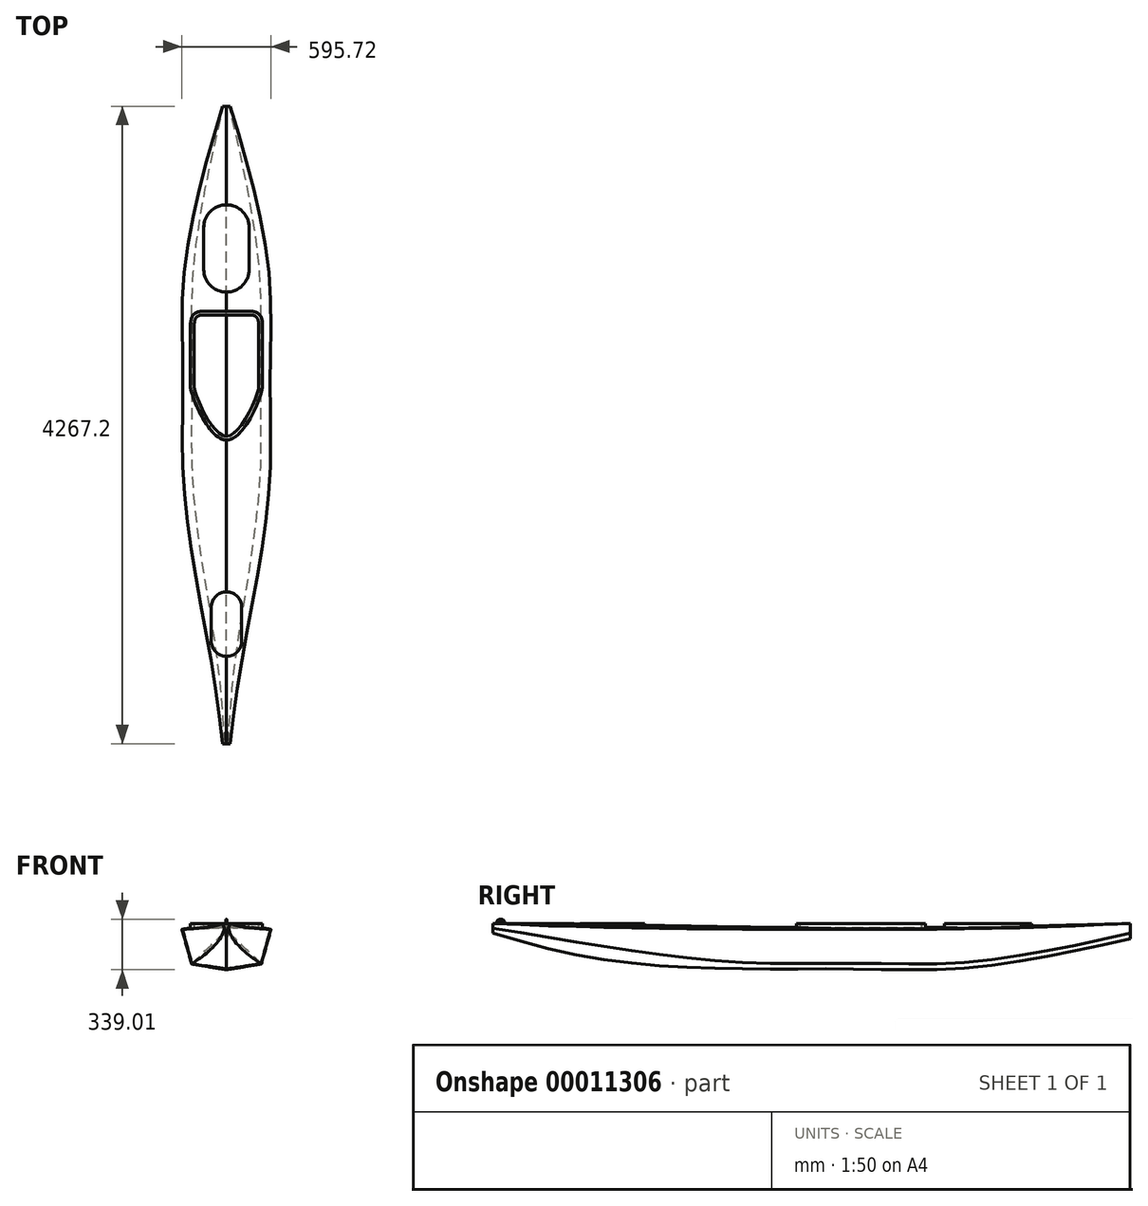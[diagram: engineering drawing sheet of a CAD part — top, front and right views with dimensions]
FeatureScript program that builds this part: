
annotation { "Feature Type Name" : "Feature", "Feature Type Description" : "" }
export const myFeature = defineFeature(function(context is Context, id is Id, definition is map)
    precondition{}
    {
        {
            var Q0;
            Q0=qCreatedBy(makeId("Front.planeOp"),FACE);
            var sketch = newSketch(context, id + "F0", { "sketchPlane" : qUnion([Q0])});
            skLineSegment(sketch, "E0", {"start": v(0, 0) * mm, "end": v(25.4, 0) * mm});
            skLineSegment(sketch, "E1", {"start": v(25.4, 0) * mm, "end": v(12.7, -31.75) * mm});
            skLineSegment(sketch, "E2.0.MirrorCS", {"start": v(0, 0) * mm, "end": v(-25.4, 0) * mm});
            skLineSegment(sketch, "E3.0.MirrorCS", {"start": v(-25.4, 0) * mm, "end": v(-12.7, -31.75) * mm});
            skPoint(sketch, "E4", {"position": v(12.7, -31.75) * mm});
            skPoint(sketch, "E5.0.MirrorP", {"position": v(-12.7, -31.75) * mm});
            skLineSegment(sketch, "E6", {"start": v(12.7, -31.75) * mm, "end": v(0, -63.5) * mm});
            skLineSegment(sketch, "E7", {"start": v(-12.7, -31.75) * mm, "end": v(0, -63.5) * mm});
            skSolve(sketch);
        }
        {
            var Q0;
            Q0=qCreatedBy(makeId("Front.planeOp"),FACE);
            cPlane(context, id + "F1", {"entities" : qUnion([Q0]), "cplaneType" : CPlaneType.OFFSET, "offset" : 304.8 * mm, "oppositeDirection" : true, "width" : 152.4 * mm, "height" : 152.4 * mm});
        }
        {
            var Q0;
            Q0=qCreatedBy(id+"F1.planeOp",FACE);
            var sketch = newSketch(context, id + "F2", { "sketchPlane" : qUnion([Q0])});
            skLineSegment(sketch, "E8", {"start": v(0, 0) * mm, "end": v(63.5, -12.7) * mm});
            skLineSegment(sketch, "E9", {"start": v(63.5, -12.7) * mm, "end": v(31.75, -82.55) * mm});
            skLineSegment(sketch, "E10.0.MirrorCS", {"start": v(0, 0) * mm, "end": v(-63.5, -12.7) * mm});
            skLineSegment(sketch, "E11.0.MirrorCS", {"start": v(-63.5, -12.7) * mm, "end": v(-31.75, -82.55) * mm});
            skPoint(sketch, "E12", {"position": v(31.75, -82.55) * mm});
            skPoint(sketch, "E13.0.MirrorP", {"position": v(-31.75, -82.55) * mm});
            skLineSegment(sketch, "E14", {"start": v(31.75, -82.55) * mm, "end": v(0, -152.4) * mm});
            skLineSegment(sketch, "E15", {"start": v(-31.75, -82.55) * mm, "end": v(0, -152.4) * mm});
            skSolve(sketch);
        }
        {
            var Q0;
            Q0=qCreatedBy(id+"F1.planeOp",FACE);
            cPlane(context, id + "F3", {"entities" : qUnion([Q0]), "cplaneType" : CPlaneType.OFFSET, "offset" : 304.8 * mm, "oppositeDirection" : true, "width" : 152.4 * mm, "height" : 152.4 * mm});
        }
        {
            var Q0;
            Q0=qCreatedBy(id+"F3.planeOp",FACE);
            var sketch = newSketch(context, id + "F4", { "sketchPlane" : qUnion([Q0])});
            skLineSegment(sketch, "E16", {"start": v(0, 0) * mm, "end": v(228.6, -25.4) * mm});
            skLineSegment(sketch, "E17", {"start": v(228.6, -25.4) * mm, "end": v(152.4, -152.4) * mm});
            skLineSegment(sketch, "E18", {"start": v(152.4, -152.4) * mm, "end": v(0, -203.2) * mm});
            skLineSegment(sketch, "E19.0.MirrorCS", {"start": v(0, 0) * mm, "end": v(-228.6, -25.4) * mm});
            skLineSegment(sketch, "E20.0.MirrorCS", {"start": v(-228.6, -25.4) * mm, "end": v(-152.4, -152.4) * mm});
            skLineSegment(sketch, "E21.0.MirrorCS", {"start": v(-152.4, -152.4) * mm, "end": v(0, -203.2) * mm});
            skSolve(sketch);
        }
        {
            var Q0;
            Q0=qCreatedBy(id+"F3.planeOp",FACE);
            cPlane(context, id + "F5", {"entities" : qUnion([Q0]), "cplaneType" : CPlaneType.OFFSET, "offset" : 304.8 * mm, "oppositeDirection" : true, "width" : 152.4 * mm, "height" : 152.4 * mm});
        }
        {
            var Q0;
            Q0=qCreatedBy(id+"F5.planeOp",FACE);
            var sketch = newSketch(context, id + "F6", { "sketchPlane" : qUnion([Q0])});
            skLineSegment(sketch, "E22", {"start": v(0, 0) * mm, "end": v(254, -31.75) * mm});
            skLineSegment(sketch, "E23", {"start": v(254, -31.75) * mm, "end": v(190.5, -190.5) * mm});
            skLineSegment(sketch, "E24", {"start": v(190.5, -190.5) * mm, "end": v(0, -241.3) * mm});
            skLineSegment(sketch, "E25.0.MirrorCS", {"start": v(0, 0) * mm, "end": v(-254, -31.75) * mm});
            skLineSegment(sketch, "E26.0.MirrorCS", {"start": v(-254, -31.75) * mm, "end": v(-190.5, -190.5) * mm});
            skLineSegment(sketch, "E27.0.MirrorCS", {"start": v(-190.5, -190.5) * mm, "end": v(0, -241.3) * mm});
            skSolve(sketch);
        }
        {
            var Q0;
            Q0=qCreatedBy(id+"F5.planeOp",FACE);
            cPlane(context, id + "F7", {"entities" : qUnion([Q0]), "cplaneType" : CPlaneType.OFFSET, "offset" : 304.8 * mm, "oppositeDirection" : true, "width" : 152.4 * mm, "height" : 152.4 * mm});
        }
        {
            var Q0;
            Q0=qCreatedBy(id+"F7.planeOp",FACE);
            var sketch = newSketch(context, id + "F8", { "sketchPlane" : qUnion([Q0])});
            skLineSegment(sketch, "E28", {"start": v(0, -12.7) * mm, "end": v(279.4, -38.1) * mm});
            skLineSegment(sketch, "E29", {"start": v(279.4, -38.1) * mm, "end": v(228.6, -203.2) * mm});
            skLineSegment(sketch, "E30", {"start": v(228.6, -203.2) * mm, "end": v(0, -266.7) * mm});
            skLineSegment(sketch, "E31.0.MirrorCS", {"start": v(0, -12.7) * mm, "end": v(-279.4, -38.1) * mm});
            skLineSegment(sketch, "E32.0.MirrorCS", {"start": v(-279.4, -38.1) * mm, "end": v(-228.6, -203.2) * mm});
            skLineSegment(sketch, "E33.0.MirrorCS", {"start": v(-228.6, -203.2) * mm, "end": v(0, -266.7) * mm});
            skSolve(sketch);
        }
        {
            var Q0;
            Q0=qCreatedBy(id+"F7.planeOp",FACE);
            cPlane(context, id + "F9", {"entities" : qUnion([Q0]), "cplaneType" : CPlaneType.OFFSET, "offset" : 304.8 * mm, "oppositeDirection" : true, "width" : 152.4 * mm, "height" : 152.4 * mm});
        }
        {
            var Q0;
            Q0=qCreatedBy(id+"F9.planeOp",FACE);
            var sketch = newSketch(context, id + "F10", { "sketchPlane" : qUnion([Q0])});
            skLineSegment(sketch, "E34", {"start": v(0, -25.4) * mm, "end": v(292.1, -38.1) * mm});
            skLineSegment(sketch, "E35", {"start": v(292.1, -38.1) * mm, "end": v(228.6, -228.6) * mm});
            skLineSegment(sketch, "E36", {"start": v(228.6, -228.6) * mm, "end": v(0, -292.1) * mm});
            skLineSegment(sketch, "E37.0.MirrorCS", {"start": v(0, -25.4) * mm, "end": v(-292.1, -38.1) * mm});
            skLineSegment(sketch, "E38.0.MirrorCS", {"start": v(-292.1, -38.1) * mm, "end": v(-228.6, -228.6) * mm});
            skLineSegment(sketch, "E39.0.MirrorCS", {"start": v(-228.6, -228.6) * mm, "end": v(0, -292.1) * mm});
            skSolve(sketch);
        }
        {
            var Q0;
            Q0=qCreatedBy(id+"F9.planeOp",FACE);
            cPlane(context, id + "F11", {"entities" : qUnion([Q0]), "cplaneType" : CPlaneType.OFFSET, "offset" : 304.8 * mm, "oppositeDirection" : true, "width" : 152.4 * mm, "height" : 152.4 * mm});
        }
        {
            var Q0;
            Q0=qCreatedBy(id+"F11.planeOp",FACE);
            var sketch = newSketch(context, id + "F12", { "sketchPlane" : qUnion([Q0])});
            skLineSegment(sketch, "E40", {"start": v(0, -25.4) * mm, "end": v(292.1, -38.1) * mm});
            skLineSegment(sketch, "E41", {"start": v(292.1, -38.1) * mm, "end": v(228.6, -266.7) * mm});
            skLineSegment(sketch, "E42", {"start": v(228.6, -266.7) * mm, "end": v(0, -304.8) * mm});
            skLineSegment(sketch, "E43.0.MirrorCS", {"start": v(0, -25.4) * mm, "end": v(-292.1, -38.1) * mm});
            skLineSegment(sketch, "E44.0.MirrorCS", {"start": v(-292.1, -38.1) * mm, "end": v(-228.6, -266.7) * mm});
            skLineSegment(sketch, "E45.0.MirrorCS", {"start": v(-228.6, -266.7) * mm, "end": v(0, -304.8) * mm});
            skSolve(sketch);
        }
        {
            var Q0;
            Q0=qCreatedBy(id+"F11.planeOp",FACE);
            cPlane(context, id + "F13", {"entities" : qUnion([Q0]), "cplaneType" : CPlaneType.OFFSET, "offset" : 304.8 * mm, "oppositeDirection" : true, "width" : 152.4 * mm, "height" : 152.4 * mm});
        }
        {
            var Q0;
            Q0=qCreatedBy(id+"F13.planeOp",FACE);
            var sketch = newSketch(context, id + "F14", { "sketchPlane" : qUnion([Q0])});
            skLineSegment(sketch, "E46.0.0", {"start": v(292.1, -38.1) * mm, "end": v(0, -25.4) * mm});
            skLineSegment(sketch, "E46.0.1", {"start": v(0, -25.4) * mm, "end": v(-292.1, -38.1) * mm});
            skLineSegment(sketch, "E46.0.2", {"start": v(-292.1, -38.1) * mm, "end": v(-228.6, -266.7) * mm});
            skLineSegment(sketch, "E46.0.3", {"start": v(-228.6, -266.7) * mm, "end": v(0, -304.8) * mm});
            skLineSegment(sketch, "E46.0.4", {"start": v(0, -304.8) * mm, "end": v(228.6, -266.7) * mm});
            skLineSegment(sketch, "E46.0.5", {"start": v(228.6, -266.7) * mm, "end": v(292.1, -38.1) * mm});
            skSolve(sketch);
        }
        {
            var Q0;
            Q0=qCreatedBy(id+"F13.planeOp",FACE);
            cPlane(context, id + "F15", {"entities" : qUnion([Q0]), "cplaneType" : CPlaneType.OFFSET, "offset" : 304.8 * mm, "oppositeDirection" : true, "width" : 152.4 * mm, "height" : 152.4 * mm});
        }
        {
            var Q0;
            Q0=qCreatedBy(id+"F15.planeOp",FACE);
            var sketch = newSketch(context, id + "F16", { "sketchPlane" : qUnion([Q0])});
            skLineSegment(sketch, "E47.0.0", {"start": v(228.6, -266.7) * mm, "end": v(292.1, -38.1) * mm});
            skLineSegment(sketch, "E47.0.1", {"start": v(292.1, -38.1) * mm, "end": v(0, -25.4) * mm});
            skLineSegment(sketch, "E47.0.2", {"start": v(0, -25.4) * mm, "end": v(-292.1, -38.1) * mm});
            skLineSegment(sketch, "E47.0.3", {"start": v(-292.1, -38.1) * mm, "end": v(-228.6, -266.7) * mm});
            skLineSegment(sketch, "E47.0.4", {"start": v(-228.6, -266.7) * mm, "end": v(0, -304.8) * mm});
            skLineSegment(sketch, "E47.0.5", {"start": v(0, -304.8) * mm, "end": v(228.6, -266.7) * mm});
            skSolve(sketch);
        }
        {
            var Q0;
            Q0=qCreatedBy(id+"F15.planeOp",FACE);
            cPlane(context, id + "F17", {"entities" : qUnion([Q0]), "cplaneType" : CPlaneType.OFFSET, "offset" : 304.8 * mm, "oppositeDirection" : true, "width" : 152.4 * mm, "height" : 152.4 * mm});
        }
        {
            var Q0;
            Q0=qCreatedBy(id+"F17.planeOp",FACE);
            var sketch = newSketch(context, id + "F18", { "sketchPlane" : qUnion([Q0])});
            skLineSegment(sketch, "E48.0.0", {"start": v(0, -304.8) * mm, "end": v(228.6, -266.7) * mm});
            skLineSegment(sketch, "E48.0.1", {"start": v(228.6, -266.7) * mm, "end": v(292.1, -38.1) * mm});
            skLineSegment(sketch, "E48.0.2", {"start": v(292.1, -38.1) * mm, "end": v(0, -25.4) * mm});
            skLineSegment(sketch, "E48.0.3", {"start": v(0, -25.4) * mm, "end": v(-292.1, -38.1) * mm});
            skLineSegment(sketch, "E48.0.4", {"start": v(-292.1, -38.1) * mm, "end": v(-228.6, -266.7) * mm});
            skLineSegment(sketch, "E48.0.5", {"start": v(-228.6, -266.7) * mm, "end": v(0, -304.8) * mm});
            skSolve(sketch);
        }
        {
            var Q0;
            Q0=qCreatedBy(id+"F17.planeOp",FACE);
            cPlane(context, id + "F19", {"entities" : qUnion([Q0]), "cplaneType" : CPlaneType.OFFSET, "offset" : 304.8 * mm, "oppositeDirection" : true, "width" : 152.4 * mm, "height" : 152.4 * mm});
        }
        {
            var Q0;
            Q0=qCreatedBy(id+"F19.planeOp",FACE);
            var sketch = newSketch(context, id + "F20", { "sketchPlane" : qUnion([Q0])});
            skLineSegment(sketch, "E49.0.0", {"start": v(-228.6, -266.7) * mm, "end": v(0, -304.8) * mm});
            skLineSegment(sketch, "E49.0.1", {"start": v(0, -304.8) * mm, "end": v(228.6, -266.7) * mm});
            skLineSegment(sketch, "E49.0.2", {"start": v(228.6, -266.7) * mm, "end": v(292.1, -38.1) * mm});
            skLineSegment(sketch, "E49.0.3", {"start": v(292.1, -38.1) * mm, "end": v(0, -25.4) * mm});
            skLineSegment(sketch, "E49.0.4", {"start": v(0, -25.4) * mm, "end": v(-292.1, -38.1) * mm});
            skLineSegment(sketch, "E49.0.5", {"start": v(-292.1, -38.1) * mm, "end": v(-228.6, -266.7) * mm});
            skSolve(sketch);
        }
        {
            var Q0;
            Q0=qCreatedBy(id+"F19.planeOp",FACE);
            cPlane(context, id + "F21", {"entities" : qUnion([Q0]), "cplaneType" : CPlaneType.OFFSET, "offset" : 1219.2 * mm, "oppositeDirection" : true, "width" : 152.4 * mm, "height" : 152.4 * mm});
        }
        {
            var Q0;
            Q0=qCreatedBy(id+"F21.planeOp",FACE);
            var sketch = newSketch(context, id + "F22", { "sketchPlane" : qUnion([Q0])});
            skLineSegment(sketch, "E50", {"start": v(0, 0) * mm, "end": v(25.4, 0) * mm});
            skLineSegment(sketch, "E51", {"start": v(25.4, 0) * mm, "end": v(19.05, -63.5) * mm});
            skLineSegment(sketch, "E52", {"start": v(19.05, -63.5) * mm, "end": v(0, -101.6) * mm});
            skLineSegment(sketch, "E53.0.MirrorCS", {"start": v(0, 0) * mm, "end": v(-25.4, 0) * mm});
            skLineSegment(sketch, "E54.0.MirrorCS", {"start": v(-25.4, 0) * mm, "end": v(-19.05, -63.5) * mm});
            skLineSegment(sketch, "E55.0.MirrorCS", {"start": v(-19.05, -63.5) * mm, "end": v(0, -101.6) * mm});
            skSolve(sketch);
        }
        {
            var Q0;
            Q0=makeQuery(id+"F0.imprint","IMPRINT",FACE,{"disambiguationData":[TD([[makeQuery(id+"F0.imprint","IMPRINT",EDGE,{"derivedFrom":sQuery(id+"F0.wireOp",EDGE,"E0")}),-1.0]])]});
            var Q1;
            Q1=makeQuery(id+"F2.imprint","IMPRINT",FACE,{"disambiguationData":[TD([[makeQuery(id+"F2.imprint","IMPRINT",EDGE,{"derivedFrom":sQuery(id+"F2.wireOp",EDGE,"E8")}),-1.0]])]});
            var Q2;
            Q2=makeQuery(id+"F12.imprint","IMPRINT",FACE,{"disambiguationData":[TD([[makeQuery(id+"F12.imprint","IMPRINT",EDGE,{"derivedFrom":sQuery(id+"F12.wireOp",EDGE,"E40")}),-1.0]])]});
            var Q3;
            Q3=makeQuery(id+"F16.imprint","IMPRINT",FACE,{"disambiguationData":[TD([[makeQuery(id+"F16.imprint","IMPRINT",EDGE,{"derivedFrom":sQuery(id+"F16.wireOp",EDGE,"E47.0.0")}),1.0]])]});
            var Q4;
            Q4=makeQuery(id+"F20.imprint","IMPRINT",FACE,{"disambiguationData":[TD([[makeQuery(id+"F20.imprint","IMPRINT",EDGE,{"derivedFrom":sQuery(id+"F20.wireOp",EDGE,"E49.0.0")}),1.0]])]});
            var Q5;
            Q5=makeQuery(id+"F22.imprint","IMPRINT",FACE,{"disambiguationData":[TD([[makeQuery(id+"F22.imprint","IMPRINT",EDGE,{"derivedFrom":sQuery(id+"F22.wireOp",EDGE,"E50")}),-1.0]])]});
            loft(context, id + "F23", {"sheetProfilesArray" : [{ "sheetProfileEntities" : qUnion([Q0]) }, { "sheetProfileEntities" : qUnion([Q1]) }, { "sheetProfileEntities" : qUnion([Q2]) }, { "sheetProfileEntities" : qUnion([Q3]) }, { "sheetProfileEntities" : qUnion([Q4]) }, { "sheetProfileEntities" : qUnion([Q5]) }]});
        }
        {
            var Q0;
            Q0=qCreatedBy(makeId("Right.planeOp"),FACE);
            var sketch = newSketch(context, id + "F24", { "sketchPlane" : qUnion([Q0])});
            skArc(sketch, "E56", {"start": v(76.2, 0) * mm, "mid": v(50.8, 25.94) * mm, "end": v(25.4, 0) * mm});
            skSolve(sketch);
        }
        {
            var Q0;
            Q0=qCreatedBy(makeId("Top.planeOp"),FACE);
            var sketch = newSketch(context, id + "F25", { "sketchPlane" : qUnion([Q0])});
            skPoint(sketch, "E57.0", {"position": v(0, 25.4) * mm});
            skCircle(sketch, "E58", {"center": v(0, 25.4) * mm, "radius": 3.18 * mm});
            skSolve(sketch);
        }
        {
            var Q0;
            Q0=qSketchRegion(id+"F25",true);
            var Q1;
            Q1=sQuery(id+"F24.wireOp",EDGE,"E56");
            sweep(context, id + "F26", {"operationType" : NewBodyOperationType.ADD, "profiles" : qUnion([Q0]), "path" : qUnion([Q1])});
        }
        {
            var Q0;
            Q0=qCreatedBy(makeId("Top.planeOp"),FACE);
            var sketch = newSketch(context, id + "F27", { "sketchPlane" : qUnion([Q0])});
            skLineSegment(sketch, "E59", {"start": v(0, 2895.6) * mm, "end": v(139.7, 2895.6) * mm});
            skLineSegment(sketch, "E60", {"start": v(241.3, 2794) * mm, "end": v(241.3, 2387.6) * mm});
            skPoint(sketch, "E61", {"position": v(241.3, 2387.6) * mm});
            skFitSpline(sketch, "E62", {"points": [v(139.7, 2895.6) * mm, v(241.3, 2794) * mm], "startDerivative": vector(228.6, 0) * mm, "endDerivative": vector(0, -228.6) * mm});
            skFitSpline(sketch, "E63", {"points": [v(241.3, 2387.6) * mm, v(0, 2032) * mm, v(-241.3, 2387.6) * mm], "startDerivative": vector(0, -304.8) * mm, "endDerivative": vector(0, 304.8) * mm});
            skLineSegment(sketch, "E64.0.MirrorCS", {"start": v(0, 2895.6) * mm, "end": v(-139.7, 2895.6) * mm});
            skFitSpline(sketch, "E65.0.MirrorCS", {"points": [v(-139.7, 2895.6) * mm, v(-241.3, 2794) * mm], "startDerivative": vector(-228.6, 0) * mm, "endDerivative": vector(0, -228.6) * mm});
            skLineSegment(sketch, "E66.0.MirrorCS", {"start": v(-241.3, 2794) * mm, "end": v(-241.3, 2387.6) * mm});
            skLineSegment(sketch, "E67.0", {"start": v(0, 2870.2) * mm, "end": v(-139.7, 2870.2) * mm});
            skLineSegment(sketch, "E67.1", {"start": v(0, 2870.2) * mm, "end": v(139.7, 2870.2) * mm});
            skFitSpline(sketch, "E67.2", {"points": [v(139.7, 2870.2) * mm, v(144.1, 2870.2) * mm, v(152.45, 2870.02) * mm, v(163.52, 2869.19) * mm, v(173.13, 2867.83) * mm, v(181.28, 2866) * mm, v(188, 2863.78) * mm, v(193.4, 2861.26) * mm, v(197.7, 2858.51) * mm, v(201.2, 2855.5) * mm, v(204.21, 2852) * mm, v(206.96, 2847.7) * mm, v(209.48, 2842.3) * mm, v(211.7, 2835.58) * mm, v(213.53, 2827.43) * mm, v(214.89, 2817.82) * mm, v(215.72, 2806.75) * mm, v(215.9, 2798.4) * mm, v(215.9, 2794) * mm]});
            skLineSegment(sketch, "E67.3", {"start": v(215.9, 2794) * mm, "end": v(215.9, 2387.6) * mm});
            skFitSpline(sketch, "E67.4", {"points": [v(215.9, 2387.6) * mm, v(215.9, 2387.43) * mm, v(215.88, 2386.78) * mm, v(215.73, 2385.04) * mm, v(215.43, 2382.7) * mm, v(214.8, 2378.9) * mm, v(213.58, 2373.03) * mm, v(211.45, 2364.52) * mm, v(208.69, 2354.76) * mm, v(204.18, 2340.3) * mm, v(197.1, 2319.87) * mm, v(186.46, 2292.58) * mm, v(173.9, 2263.39) * mm, v(159.63, 2233.19) * mm, v(143.84, 2202.84) * mm, v(126.75, 2173.2) * mm, v(108.6, 2145.15) * mm, v(89.68, 2119.56) * mm, v(73.53, 2101.04) * mm, v(60.62, 2088.33) * mm, v(51.02, 2079.96) * mm, v(41.58, 2072.85) * mm, v(32.4, 2067.05) * mm, v(25.06, 2063.36) * mm, v(19.41, 2061.1) * mm, v(15.3, 2059.72) * mm, v(11.3, 2058.67) * mm, v(7.44, 2057.93) * mm, v(4.3, 2057.57) * mm, v(1.83, 2057.42) * mm, v(0, 2057.39) * mm, v(-1.83, 2057.42) * mm, v(-4.3, 2057.57) * mm, v(-7.44, 2057.93) * mm, v(-11.3, 2058.67) * mm, v(-15.3, 2059.72) * mm, v(-19.41, 2061.1) * mm, v(-25.06, 2063.36) * mm, v(-32.4, 2067.05) * mm, v(-41.58, 2072.85) * mm, v(-51.02, 2079.96) * mm, v(-60.62, 2088.33) * mm, v(-73.53, 2101.04) * mm, v(-89.68, 2119.56) * mm, v(-108.6, 2145.15) * mm, v(-126.75, 2173.2) * mm, v(-143.84, 2202.84) * mm, v(-159.63, 2233.19) * mm, v(-173.9, 2263.39) * mm, v(-186.46, 2292.58) * mm, v(-197.1, 2319.87) * mm, v(-204.18, 2340.3) * mm, v(-208.69, 2354.76) * mm, v(-211.45, 2364.52) * mm, v(-213.58, 2373.03) * mm, v(-214.8, 2378.9) * mm, v(-215.43, 2382.7) * mm, v(-215.73, 2385.04) * mm, v(-215.88, 2386.78) * mm, v(-215.9, 2387.43) * mm, v(-215.9, 2387.6) * mm]});
            skFitSpline(sketch, "E67.5", {"points": [v(-139.7, 2870.2) * mm, v(-144.1, 2870.2) * mm, v(-152.45, 2870.02) * mm, v(-163.52, 2869.19) * mm, v(-173.13, 2867.83) * mm, v(-181.28, 2866) * mm, v(-188, 2863.78) * mm, v(-193.4, 2861.26) * mm, v(-197.7, 2858.51) * mm, v(-201.2, 2855.5) * mm, v(-204.21, 2852) * mm, v(-206.96, 2847.7) * mm, v(-209.48, 2842.3) * mm, v(-211.7, 2835.58) * mm, v(-213.53, 2827.43) * mm, v(-214.89, 2817.82) * mm, v(-215.72, 2806.75) * mm, v(-215.9, 2798.4) * mm, v(-215.9, 2794) * mm]});
            skLineSegment(sketch, "E67.6", {"start": v(-215.9, 2794) * mm, "end": v(-215.9, 2387.6) * mm});
            skFitSpline(sketch, "E68.0", {"points": [v(0, 3048) * mm, v(0, 3454.4) * mm, v(0, 3860.8) * mm, v(0, 4267.2) * mm], "construction": true});
            skArc(sketch, "E69", {"start": v(-152.4, 3175) * mm, "mid": v(-107.76, 3067.24) * mm, "end": v(0, 3022.6) * mm});
            skArc(sketch, "E70", {"start": v(0, 3606.8) * mm, "mid": v(-107.76, 3562.16) * mm, "end": v(-152.4, 3454.4) * mm});
            skLineSegment(sketch, "E71", {"start": v(-152.4, 3175) * mm, "end": v(-152.4, 3454.4) * mm});
            skArc(sketch, "E72.0.MirrorCS", {"start": v(152.4, 3175) * mm, "mid": v(107.76, 3067.24) * mm, "end": v(0, 3022.6) * mm});
            skLineSegment(sketch, "E73.0.MirrorCS", {"start": v(152.4, 3175) * mm, "end": v(152.4, 3454.4) * mm});
            skArc(sketch, "E74.0.MirrorCS", {"start": v(0, 3606.8) * mm, "mid": v(107.76, 3562.16) * mm, "end": v(152.4, 3454.4) * mm});
            skArc(sketch, "E75", {"start": v(-101.6, 685.8) * mm, "mid": v(-71.84, 613.96) * mm, "end": v(0, 584.2) * mm});
            skLineSegment(sketch, "E76", {"start": v(-101.6, 685.8) * mm, "end": v(-101.6, 914.4) * mm});
            skArc(sketch, "E77", {"start": v(0, 1016) * mm, "mid": v(-71.84, 986.24) * mm, "end": v(-101.6, 914.4) * mm});
            skArc(sketch, "E78.0.MirrorCS", {"start": v(101.6, 685.8) * mm, "mid": v(71.84, 613.96) * mm, "end": v(0, 584.2) * mm});
            skLineSegment(sketch, "E79.0.MirrorCS", {"start": v(101.6, 685.8) * mm, "end": v(101.6, 914.4) * mm});
            skArc(sketch, "E80.0.MirrorCS", {"start": v(0, 1016) * mm, "mid": v(71.84, 986.24) * mm, "end": v(101.6, 914.4) * mm});
            skSolve(sketch);
        }
        {
            var Q0;
            Q0=qSketchRegion(id+"F27",true);
            var Q1;
            Q1=makeQuery(id+"F23.opLoft","SWEPT_FACE",FACE,{"disambiguationData":[OSD([sQuery(id+"F0.wireOp",EDGE,"E0"),sQuery(id+"F0.wireOp",EDGE,"E1"),sQuery(id+"F0.wireOp",EDGE,"E2.0.MirrorCS"),sQuery(id+"F2.wireOp",EDGE,"E8"),sQuery(id+"F2.wireOp",EDGE,"E9"),sQuery(id+"F2.wireOp",EDGE,"E10.0.MirrorCS")])]});
            extrude(context, id + "F28", {"entities" : qUnion([Q0]), "operationType" : NewBodyOperationType.ADD, "endBound" : BoundingType.UP_TO_BODY, "oppositeDirection" : true, "endBoundEntityBody" : qUnion([Q1]), "depth" : 25.4 * mm});
        }
    });
